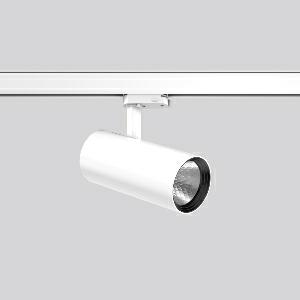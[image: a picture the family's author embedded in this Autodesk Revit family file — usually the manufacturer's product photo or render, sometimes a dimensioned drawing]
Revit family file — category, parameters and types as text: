
# Revit family: deecos_s_mini_742197_002_3_76_6aba
name_source: partatom
category: Lighting Fixtures
units: mm (PartAtom-declared; Revit-internal decimal feet)

## family parameters
Cut with Voids When Loaded = No
Host = Face
Light Source = No
Part Type = Normal
Room Calculation Point = No
Round Connector Dimension = Use Diameter
Shared = No

## types (1)
- DEECOS S mini (1 x LED Modul 935, 2650 lm, 3500)
    Apparent Load = 20 VA
    Approval mark = CE
    CIE Flux Codes = 95 99 100 100 100
    Color Rendering = 92
    Color Temperature = 3500
    Default Elevation = 1800 mm
    Description = Series: DEECOS S mini
LED surface-mounted projector in modern design with no visible cooling ribs. Housing: die-cast aluminium, powder-coated. Rotation range: 356°. Swivel range: 90°. Black plastic ring and recessed LED to prevent glare from the side. Optical assembly with reflector made of MIRO-Silver with 98% total light reflection for outstanding efficiency - can be changed without tools. Best colour rendering index Ra>90. With adapter for RZB 3-circuit DALI tracks. Suitable for Track on ceiling, Wall track. High quality converter without flickering and stroboscopic effect. The following accessories can be mounted without use of tools: interchangeable lenses, decorative glasses, honeycomb louvre, clear and frosted diffusers, white interchangeable plastic ring. 
Colour: traffic white, matt (RAL 9016)
Diameter: 87 mm
Height: 214 mm
Lamp: LED
Socket: without socket
Colour temperature: 3500K
Colour rendering index (CRI): 92
System power: 20 W
Rated luminous flux: 2650 lm
Luminous efficiency: 133 lm/W
Control gear: Converter, dimmable, DALI
Protection class: I
Type of protection: IP 20
    Height = 214 mm
    Lamp = 1 x LED Modul 935
    Lamp Light Flux = 2650 lm
    Lamp count = 1
    Length = 87 mm
    Lifetime = 50000 h
    Luminous efficacy = 133 lm/W
    Manufacturer = RZB
    ModVariant = No
    Model = 742197.002.3.76
    Mounting Place = Ceiling
    Mounting Type = Rail mounted
    Number of Poles = 1
    OnlyDefault = Yes
    Power Factor = 1
    Product Name = DEECOS S mini
    Product group = Track mounted projectors
    ProductGroupID = 301
    Protection Class = Protection class I
    Protection Degree = IP 20
    RLX_Detail_Level = 1
    RLX_Emergency_Light_Flux = 0 lm
    RLX_Emergency_Type = 0
    RLX_Emergency_Type_DB = No
    RlxData = <blob elided: 35641 chars, md5=5bdca4b6>
    Socket = socket
    Standby Power = 0 W
    System Light Flux = 2650 lm
    System Power = 20 W
    Type Comments = Product without accessories
    Type Image = 741926.002.jpg
    URL = http://relux.com
    VarID = ---
    Voltage = 230 V
    Voltage Range = 220-240 V
    Weight = 0.00 kg
    Width = 0 mm  [stored 0 ft]

note: [stored X ft] marks values corroborated as IEEE doubles in the binary element streams (Revit-internal decimal feet)

## geometry (parser evidence)
native form markers: Blend x4, Sweep x14
no freeform markers — native parametric forms only
